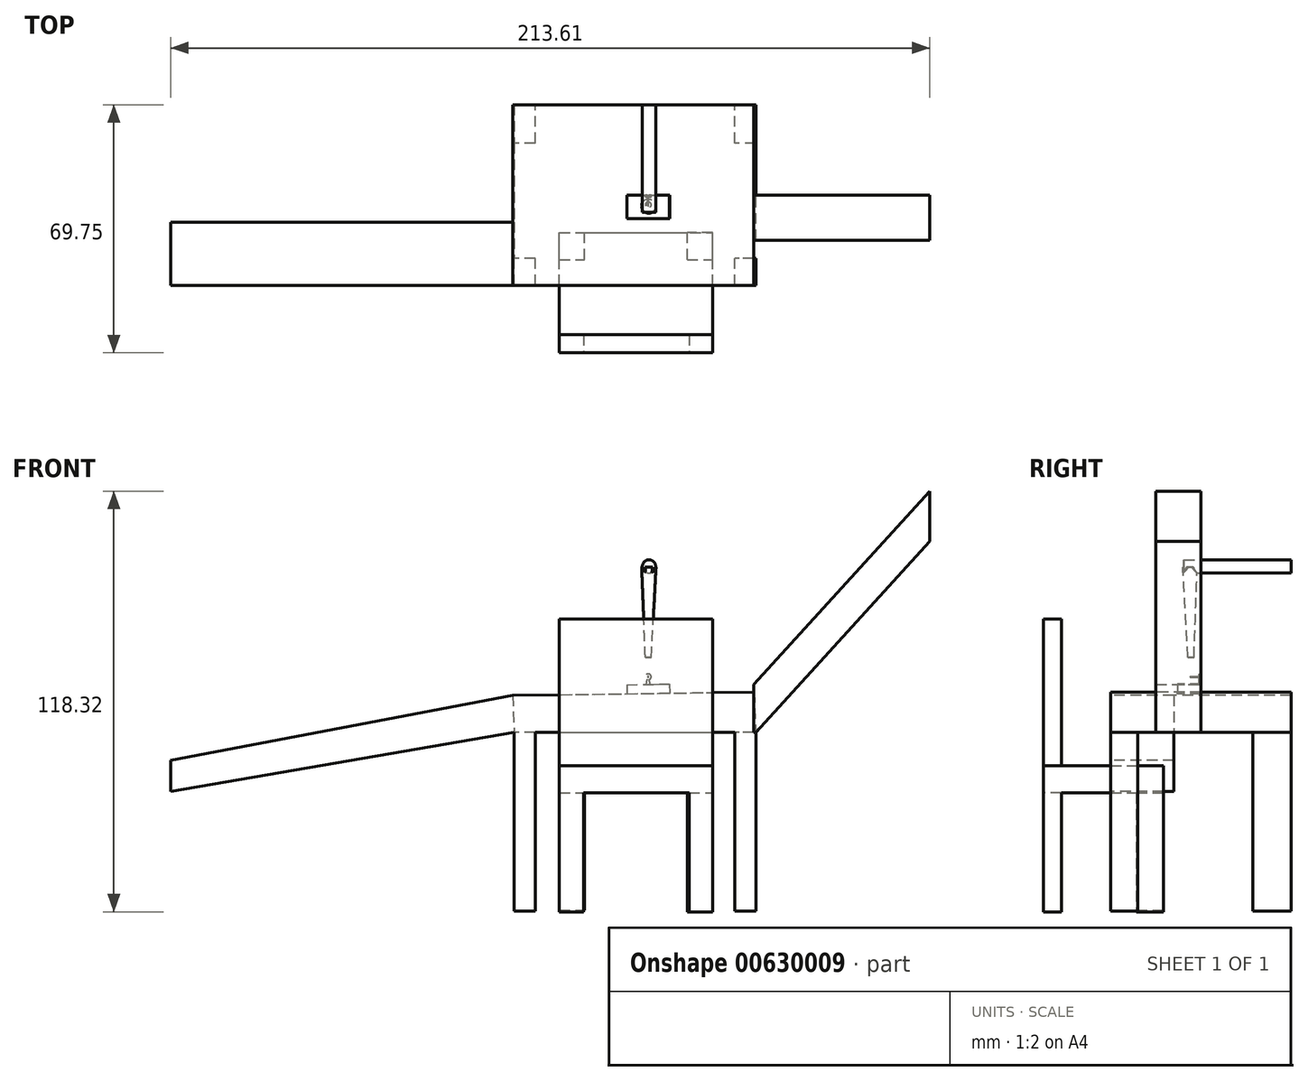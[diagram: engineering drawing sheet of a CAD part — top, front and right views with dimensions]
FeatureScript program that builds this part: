
annotation { "Feature Type Name" : "Feature", "Feature Type Description" : "" }
export const myFeature = defineFeature(function(context is Context, id is Id, definition is map)
    precondition{}
    {
        {
            var Q0;
            Q0=qCreatedBy(makeId("Front.planeOp"),FACE);
            var sketch = newSketch(context, id + "F0", { "sketchPlane" : qUnion([Q0])});
            skLineSegment(sketch, "E0", {"start": v(61.58, 0) * mm, "end": v(111.12, 54.36) * mm});
            skLineSegment(sketch, "E1", {"start": v(111.12, 54.36) * mm, "end": v(111.12, 40.27) * mm});
            skLineSegment(sketch, "E2", {"start": v(111.12, 40.27) * mm, "end": v(62.19, -13.43) * mm});
            skLineSegment(sketch, "E3", {"start": v(62.19, -13.43) * mm, "end": v(0, -13.43) * mm});
            skLineSegment(sketch, "E4", {"start": v(0, -13.43) * mm, "end": v(0, 0) * mm});
            skLineSegment(sketch, "E5", {"start": v(0, 0) * mm, "end": v(61.58, 0) * mm});
            skLineSegment(sketch, "E6", {"start": v(61.58, 0) * mm, "end": v(62.19, -13.43) * mm});
            skSolve(sketch);
        }
        {
            var Q0;
            Q0=makeQuery(id+"F0.imprint","IMPRINT",FACE,{"disambiguationData":[TD([[makeQuery(id+"F0.imprint","IMPRINT",EDGE,{"derivedFrom":sQuery(id+"F0.wireOp",EDGE,"E0")}),-1.0]])]});
            extrude(context, id + "F1", {"entities" : qUnion([Q0]), "depth" : 12.7 * mm, "offsetDistance" : 25.4 * mm});
        }
        {
            var Q0;
            Q0=makeQuery(id+"F1.opExtrude","CAP_FACE",FACE,{"disambiguationData":[OSD([sQuery(id+"F0.wireOp",EDGE,"E0"),sQuery(id+"F0.wireOp",EDGE,"E1"),sQuery(id+"F0.wireOp",EDGE,"E2"),sQuery(id+"F0.wireOp",EDGE,"E6")])],"isStart":false});
            var sketch = newSketch(context, id + "F2", { "sketchPlane" : qUnion([Q0])});
            skLineSegment(sketch, "E7", {"start": v(61.58, 0) * mm, "end": v(-6.26, -3.07) * mm});
            skLineSegment(sketch, "E8", {"start": v(-6.26, -3.07) * mm, "end": v(-5.79, -13.43) * mm});
            skLineSegment(sketch, "E9", {"start": v(-5.79, -13.43) * mm, "end": v(62.19, -13.43) * mm});
            skLineSegment(sketch, "E10", {"start": v(62.19, -13.43) * mm, "end": v(61.58, 0) * mm});
            skSolve(sketch);
        }
        {
            var Q0;
            Q0=makeQuery(id+"F2.imprint","IMPRINT",FACE,{"disambiguationData":[TD([[makeQuery(id+"F2.imprint","IMPRINT",EDGE,{"derivedFrom":sQuery(id+"F2.wireOp",EDGE,"E7")}),1.0]])]});
            extrude(context, id + "F3", {"entities" : qUnion([Q0]), "operationType" : NewBodyOperationType.ADD, "oppositeDirection" : true, "depth" : 38.1 * mm, "offsetDistance" : 25.4 * mm});
        }
        {
            var Q0;
            Q0=makeQuery(id+"F3.boolean.opBoolean","MERGE",FACE,{"derivedFrom":[makeQuery(id+"F1.opExtrude","CAP_FACE",FACE,{"disambiguationData":[OSD([sQuery(id+"F0.wireOp",EDGE,"E0"),sQuery(id+"F0.wireOp",EDGE,"E1"),sQuery(id+"F0.wireOp",EDGE,"E2"),sQuery(id+"F0.wireOp",EDGE,"E6")])],"isStart":false}),makeQuery(id+"F3.opExtrude","CAP_FACE",FACE,{"disambiguationData":[OSD([sQuery(id+"F2.wireOp",EDGE,"E7"),sQuery(id+"F2.wireOp",EDGE,"E8"),sQuery(id+"F2.wireOp",EDGE,"E9"),sQuery(id+"F2.wireOp",EDGE,"E10")])],"isStart":true})]});
            var sketch = newSketch(context, id + "F4", { "sketchPlane" : qUnion([Q0])});
            skLineSegment(sketch, "E11", {"start": v(61.58, 0) * mm, "end": v(61.58, -13.43) * mm});
            skLineSegment(sketch, "E12", {"start": v(61.58, -13.43) * mm, "end": v(-5.79, -13.43) * mm});
            skLineSegment(sketch, "E13", {"start": v(-5.79, -13.43) * mm, "end": v(-6.26, -3.07) * mm});
            skLineSegment(sketch, "E14", {"start": v(-6.26, -3.07) * mm, "end": v(61.58, 0) * mm});
            skSolve(sketch);
        }
        {
            var Q0;
            Q0=makeQuery(id+"F4.imprint","IMPRINT",FACE,{"disambiguationData":[TD([[makeQuery(id+"F4.imprint","IMPRINT",EDGE,{"derivedFrom":sQuery(id+"F4.wireOp",EDGE,"E11")}),-1.0]])]});
            extrude(context, id + "F5", {"entities" : qUnion([Q0]), "operationType" : NewBodyOperationType.ADD, "depth" : 12.7 * mm, "offsetDistance" : 25.4 * mm});
        }
        {
            var Q0;
            Q0=makeQuery(id+"F5.opExtrude","CAP_FACE",FACE,{"disambiguationData":[OSD([sQuery(id+"F4.wireOp",EDGE,"E11"),sQuery(id+"F4.wireOp",EDGE,"E12"),sQuery(id+"F4.wireOp",EDGE,"E13"),sQuery(id+"F4.wireOp",EDGE,"E14")])],"isStart":false});
            var sketch = newSketch(context, id + "F6", { "sketchPlane" : qUnion([Q0])});
            skLineSegment(sketch, "E15", {"start": v(-6.26, -3.07) * mm, "end": v(61.58, -2.1) * mm});
            skLineSegment(sketch, "E16", {"start": v(61.58, -2.1) * mm, "end": v(61.58, 0) * mm});
            skLineSegment(sketch, "E17", {"start": v(61.58, 0) * mm, "end": v(-6.26, -3.07) * mm});
            skSolve(sketch);
        }
        {
            var Q0;
            Q0=makeQuery(id+"F6.imprint","IMPRINT",FACE,{"disambiguationData":[TD([[makeQuery(id+"F6.imprint","IMPRINT",EDGE,{"derivedFrom":sQuery(id+"F6.wireOp",EDGE,"E15")}),1.0]])]});
            extrude(context, id + "F7", {"entities" : qUnion([Q0]), "operationType" : NewBodyOperationType.REMOVE, "oppositeDirection" : true, "depth" : 127 * mm, "offsetDistance" : 25.4 * mm});
        }
        {
            var Q0;
            Q0=makeQuery(id+"F7.boolean.opBoolean","COPY",FACE,{"derivedFrom":makeQuery(id+"F7.opExtrude","SWEPT_FACE",FACE,{"disambiguationData":[OSD([sQuery(id+"F6.wireOp",EDGE,"E16")])]})});
            var sketch = newSketch(context, id + "F8", { "sketchPlane" : qUnion([Q0])});
            skLineSegment(sketch, "E18", {"start": v(12.7, 0) * mm, "end": v(-25.4, 0) * mm});
            skLineSegment(sketch, "E19", {"start": v(-25.4, 0) * mm, "end": v(-25.4, -2.1) * mm});
            skLineSegment(sketch, "E20", {"start": v(-25.4, -2.1) * mm, "end": v(12.7, -2.1) * mm});
            skLineSegment(sketch, "E21", {"start": v(12.7, -2.1) * mm, "end": v(12.7, 0) * mm});
            skLineSegment(sketch, "E22", {"start": v(0, 0) * mm, "end": v(0, -2.1) * mm});
            skSolve(sketch);
        }
        {
            var Q0;
            {var subQ0=sQuery(id+"F8.wireOp",EDGE,"E19");Q0=makeQuery(id+"F8.imprint","IMPRINT",FACE,{"disambiguationData":[TD([[makeQuery(id+"F8.imprint","IMPRINT",EDGE,{"derivedFrom":subQ0}),1.0]])]});}
            extrude(context, id + "F9", {"entities" : qUnion([Q0]), "operationType" : NewBodyOperationType.REMOVE, "oppositeDirection" : true, "depth" : 25.4 * mm, "offsetDistance" : 25.4 * mm});
        }
        {
            var Q0;
            Q0=makeQuery(id+"F7.boolean.opBoolean","COPY",FACE,{"derivedFrom":makeQuery(id+"F7.opExtrude","SWEPT_FACE",FACE,{"disambiguationData":[OSD([sQuery(id+"F6.wireOp",EDGE,"E15")])]})});
            var sketch = newSketch(context, id + "F10", { "sketchPlane" : qUnion([Q0])});
            skLineSegment(sketch, "E23.bottom", {"start": v(25.86, 0) * mm, "end": v(37.88, 0) * mm});
            skLineSegment(sketch, "E23.top", {"start": v(25.86, -9.18) * mm, "end": v(37.88, -9.18) * mm});
            skLineSegment(sketch, "E23.left", {"start": v(25.86, 0) * mm, "end": v(25.86, -9.18) * mm});
            skLineSegment(sketch, "E23.right", {"start": v(37.88, 0) * mm, "end": v(37.88, -9.18) * mm});
            skSolve(sketch);
        }
        {
            var Q0;
            Q0=makeQuery(id+"F10.imprint","IMPRINT",FACE,{"disambiguationData":[TD([[makeQuery(id+"F10.imprint","IMPRINT",EDGE,{"derivedFrom":sQuery(id+"F10.wireOp",EDGE,"E23.bottom")}),-1.0]])]});
            extrude(context, id + "F11", {"entities" : qUnion([Q0]), "operationType" : NewBodyOperationType.ADD, "depth" : 2.54 * mm, "offsetDistance" : 25.4 * mm});
        }
        {
            var Q0;
            Q0=makeQuery(id+"F11.opExtrude","SWEPT_FACE",FACE,{"disambiguationData":[OSD([sQuery(id+"F10.wireOp",EDGE,"E23.bottom")])]});
            var sketch = newSketch(context, id + "F12", { "sketchPlane" : qUnion([Q0])});
            skLineSegment(sketch, "E24", {"start": v(-31.91, -2.53) * mm, "end": v(-31.91, 2.15) * mm});
            skCircle(sketch, "E25", {"center": v(-31.91, 2.15) * mm, "radius": 0.83 * mm});
            skLineSegment(sketch, "E26", {"start": v(-31.91, -2.53) * mm, "end": v(-33.19, -2.5) * mm});
            skLineSegment(sketch, "E27", {"start": v(-33.19, -2.5) * mm, "end": v(-31.91, 2.15) * mm});
            skLineSegment(sketch, "E28.MirrorCS", {"start": v(-30.64, -2.5) * mm, "end": v(-31.91, 2.15) * mm});
            skLineSegment(sketch, "E29.MirrorCS", {"start": v(-31.91, -2.53) * mm, "end": v(-30.64, -2.5) * mm});
            skSolve(sketch);
        }
        {
            var Q0;
            {var subQ0=sQuery(id+"F12.wireOp",EDGE,"E25");var subQ1=sQuery(id+"F12.wireOp",EDGE,"E24");var subQ2=makeQuery(id+"F12.imprint","INTERSECT",VERTEX,{"derivedFrom":[subQ1,subQ0]});Q0=makeQuery(id+"F12.imprint","IMPRINT",FACE,{"disambiguationData":[TD([[makeQuery(id+"F12.imprint","IMPRINT",EDGE,{"disambiguationData":[TD([[subQ2,1.0]])],"derivedFrom":subQ1}),-1.0]])]});}
            var Q1;
            {var subQ0=sQuery(id+"F12.wireOp",EDGE,"E25");var subQ1=sQuery(id+"F12.wireOp",EDGE,"E24");var subQ2=makeQuery(id+"F12.imprint","INTERSECT",VERTEX,{"derivedFrom":[subQ1,subQ0]});Q1=makeQuery(id+"F12.imprint","IMPRINT",FACE,{"disambiguationData":[TD([[makeQuery(id+"F12.imprint","IMPRINT",EDGE,{"disambiguationData":[TD([[subQ2,1.0]])],"derivedFrom":subQ1}),1.0]])]});}
            var Q2;
            {var subQ0=sQuery(id+"F12.wireOp",EDGE,"E27");var subQ3=sQuery(id+"F12.wireOp",EDGE,"E25");var subQ5=makeQuery(id+"F12.imprint","INTERSECT",VERTEX,{"derivedFrom":[subQ3,subQ0]});Q2=makeQuery(id+"F12.imprint","IMPRINT",FACE,{"disambiguationData":[TD([[makeQuery(id+"F12.imprint","IMPRINT",EDGE,{"disambiguationData":[TD([[subQ5,-1.0]])],"derivedFrom":subQ3}),1.0]])]});}
            var Q3;
            {var subQ0=sQuery(id+"F12.wireOp",EDGE,"E28.MirrorCS");var subQ3=sQuery(id+"F12.wireOp",EDGE,"E25");var subQ5=makeQuery(id+"F12.imprint","INTERSECT",VERTEX,{"derivedFrom":[subQ3,subQ0]});Q3=makeQuery(id+"F12.imprint","IMPRINT",FACE,{"disambiguationData":[TD([[makeQuery(id+"F12.imprint","IMPRINT",EDGE,{"disambiguationData":[TD([[subQ5,1.0]])],"derivedFrom":subQ3}),1.0]])]});}
            var Q4;
            {var subQ0=sQuery(id+"F12.wireOp",EDGE,"E27");var subQ1=sQuery(id+"F12.wireOp",EDGE,"E25");var subQ2=makeQuery(id+"F12.imprint","INTERSECT",VERTEX,{"derivedFrom":[subQ1,subQ0]});Q4=makeQuery(id+"F12.imprint","IMPRINT",FACE,{"disambiguationData":[TD([[makeQuery(id+"F12.imprint","IMPRINT",EDGE,{"disambiguationData":[TD([[subQ2,1.0]])],"derivedFrom":subQ1}),1.0]])]});}
            extrude(context, id + "F13", {"entities" : qUnion([Q0, Q1, Q2, Q3, Q4]), "operationType" : NewBodyOperationType.ADD, "oppositeDirection" : true, "depth" : 0.5 * mm, "offsetDistance" : 25.4 * mm});
        }
        {
            var Q0;
            Q0=makeQuery(id+"F13.opExtrude","CAP_FACE",FACE,{"disambiguationData":[OSD([sQuery(id+"F10.wireOp",EDGE,"E23.bottom"),sQuery(id+"F12.wireOp",EDGE,"E25"),sQuery(id+"F12.wireOp",EDGE,"E27"),sQuery(id+"F12.wireOp",EDGE,"E28.MirrorCS")])],"isStart":false});
            var sketch = newSketch(context, id + "F14", { "sketchPlane" : qUnion([Q0])});
            skCircle(sketch, "E30", {"center": v(31.91, 2.15) * mm, "radius": 0.16 * mm});
            skSolve(sketch);
        }
        {
            var Q0;
            Q0=makeQuery(id+"F14.imprint","IMPRINT",FACE,{"disambiguationData":[TD([[makeQuery(id+"F14.imprint","IMPRINT",EDGE,{"derivedFrom":sQuery(id+"F14.wireOp",EDGE,"E30")}),1.0]])]});
            extrude(context, id + "F15", {"entities" : qUnion([Q0]), "operationType" : NewBodyOperationType.ADD, "depth" : 2.54 * mm, "offsetDistance" : 25.4 * mm});
        }
        {
            var Q0;
            Q0=makeQuery(id+"F11.opExtrude","SWEPT_FACE",FACE,{"disambiguationData":[OSD([sQuery(id+"F10.wireOp",EDGE,"E23.top")])]});
            extrude(context, id + "F16", {"entities" : qUnion([Q0]), "operationType" : NewBodyOperationType.REMOVE, "oppositeDirection" : true, "depth" : 2.54 * mm, "offsetDistance" : 25.4 * mm});
        }
        {
            var Q0;
            Q0=makeQuery(id+"F3.opExtrude","CAP_FACE",FACE,{"disambiguationData":[OSD([sQuery(id+"F2.wireOp",EDGE,"E7"),sQuery(id+"F2.wireOp",EDGE,"E8"),sQuery(id+"F2.wireOp",EDGE,"E9"),sQuery(id+"F2.wireOp",EDGE,"E10")])],"isStart":false});
            var sketch = newSketch(context, id + "F17", { "sketchPlane" : qUnion([Q0])});
            skLineSegment(sketch, "E31", {"start": v(-62.19, -13.43) * mm, "end": v(-62.19, -63.77) * mm});
            skLineSegment(sketch, "E32", {"start": v(-62.19, -63.77) * mm, "end": v(-56.29, -63.77) * mm});
            skLineSegment(sketch, "E33", {"start": v(-56.29, -63.77) * mm, "end": v(-56.29, -13.43) * mm});
            skLineSegment(sketch, "E34", {"start": v(-56.29, -13.43) * mm, "end": v(-62.19, -13.43) * mm});
            skLineSegment(sketch, "E35", {"start": v(-28.2, -13.43) * mm, "end": v(-28.2, -2.58) * mm});
            skLineSegment(sketch, "E36.MirrorCS", {"start": v(-0.11, -63.77) * mm, "end": v(-0.11, -13.43) * mm});
            skLineSegment(sketch, "E37.MirrorCS", {"start": v(5.79, -13.43) * mm, "end": v(5.79, -63.77) * mm});
            skLineSegment(sketch, "E38.MirrorCS", {"start": v(5.79, -63.77) * mm, "end": v(-0.11, -63.77) * mm});
            skSolve(sketch);
        }
        {
            var Q0;
            {var subQ0=sQuery(id+"F17.wireOp",EDGE,"E36.MirrorCS");Q0=makeQuery(id+"F17.imprint","IMPRINT",FACE,{"disambiguationData":[TD([[makeQuery(id+"F17.imprint","IMPRINT",EDGE,{"derivedFrom":subQ0}),-1.0]])]});}
            var Q1;
            Q1=makeQuery(id+"F17.imprint","IMPRINT",FACE,{"disambiguationData":[TD([[makeQuery(id+"F17.imprint","IMPRINT",EDGE,{"derivedFrom":sQuery(id+"F17.wireOp",EDGE,"E31")}),1.0]])]});
            extrude(context, id + "F18", {"entities" : qUnion([Q0, Q1]), "operationType" : NewBodyOperationType.ADD, "oppositeDirection" : true, "depth" : 50.8 * mm, "offsetDistance" : 25.4 * mm});
        }
        {
            var Q0;
            Q0=makeQuery(id+"F18.opExtrude","SWEPT_FACE",FACE,{"disambiguationData":[OSD([sQuery(id+"F17.wireOp",EDGE,"E37.MirrorCS")])]});
            var sketch = newSketch(context, id + "F19", { "sketchPlane" : qUnion([Q0])});
            skLineSegment(sketch, "E39", {"start": v(17.83, -63.77) * mm, "end": v(17.83, -13.43) * mm});
            skLineSegment(sketch, "E40", {"start": v(17.83, -13.43) * mm, "end": v(-14.62, -13.43) * mm});
            skLineSegment(sketch, "E41", {"start": v(-14.62, -13.43) * mm, "end": v(-14.62, -63.77) * mm});
            skLineSegment(sketch, "E42", {"start": v(-14.62, -63.77) * mm, "end": v(17.83, -63.77) * mm});
            skSolve(sketch);
        }
        {
            var Q0;
            Q0=makeQuery(id+"F19.imprint","IMPRINT",FACE,{"disambiguationData":[TD([[makeQuery(id+"F19.imprint","IMPRINT",EDGE,{"derivedFrom":sQuery(id+"F19.wireOp",EDGE,"E39")}),1.0]])]});
            extrude(context, id + "F20", {"entities" : qUnion([Q0]), "operationType" : NewBodyOperationType.REMOVE, "oppositeDirection" : true, "depth" : 304.8 * mm, "offsetDistance" : 25.4 * mm});
        }
        {
            var Q0;
            Q0=makeQuery(id+"F18.boolean.opBoolean","MERGE",FACE,{"derivedFrom":[makeQuery(id+"F5.opExtrude","CAP_FACE",FACE,{"disambiguationData":[OSD([sQuery(id+"F4.wireOp",EDGE,"E11"),sQuery(id+"F4.wireOp",EDGE,"E12"),sQuery(id+"F4.wireOp",EDGE,"E13"),sQuery(id+"F4.wireOp",EDGE,"E14")])],"isStart":false}),makeQuery(id+"F18.opExtrude","CAP_FACE",FACE,{"disambiguationData":[OSD([sQuery(id+"F17.wireOp",EDGE,"E31"),sQuery(id+"F17.wireOp",EDGE,"E32"),sQuery(id+"F17.wireOp",EDGE,"E33"),sQuery(id+"F17.wireOp",EDGE,"E34")])],"isStart":false}),makeQuery(id+"F18.opExtrude","CAP_FACE",FACE,{"disambiguationData":[OSD([sQuery(id+"F2.wireOp",EDGE,"E9"),sQuery(id+"F17.wireOp",EDGE,"E36.MirrorCS"),sQuery(id+"F17.wireOp",EDGE,"E37.MirrorCS"),sQuery(id+"F17.wireOp",EDGE,"E38.MirrorCS")])],"isStart":false})]});
            var sketch = newSketch(context, id + "F21", { "sketchPlane" : qUnion([Q0])});
            skLineSegment(sketch, "E43", {"start": v(-6.26, -3.07) * mm, "end": v(-102.5, -21.32) * mm});
            skLineSegment(sketch, "E44", {"start": v(-102.5, -21.32) * mm, "end": v(-102.5, -30.14) * mm});
            skLineSegment(sketch, "E45", {"start": v(-102.5, -30.14) * mm, "end": v(-5.79, -13.43) * mm});
            skLineSegment(sketch, "E46", {"start": v(-5.79, -13.43) * mm, "end": v(-6.26, -3.07) * mm});
            skSolve(sketch);
        }
        {
            var Q0;
            Q0 = qSketchRegion(id + "F21", true);
            extrude(context, id + "F22", {"entities" : qUnion([Q0]), "operationType" : NewBodyOperationType.ADD, "oppositeDirection" : true, "depth" : 17.78 * mm, "offsetDistance" : 25.4 * mm});
        }
        {
            var Q0;
            Q0=qCreatedBy(makeId("Top.planeOp"),FACE);
            cPlane(context, id + "F23", {"entities" : qUnion([Q0]), "cplaneType" : CPlaneType.OFFSET, "offset" : 22.86 * mm, "oppositeDirection" : true, "width" : 152.4 * mm, "height" : 152.4 * mm});
        }
        {
            var Q0;
            Q0=qCreatedBy(id+"F23.planeOp",FACE);
            var sketch = newSketch(context, id + "F24", { "sketchPlane" : qUnion([Q0])});
            skLineSegment(sketch, "E47.bottom", {"start": v(6.89, -44.35) * mm, "end": v(50.02, -44.35) * mm});
            skLineSegment(sketch, "E47.top", {"start": v(6.89, -10.54) * mm, "end": v(50.02, -10.54) * mm});
            skLineSegment(sketch, "E47.left", {"start": v(6.89, -44.35) * mm, "end": v(6.89, -10.54) * mm});
            skLineSegment(sketch, "E47.right", {"start": v(50.02, -44.35) * mm, "end": v(50.02, -10.54) * mm});
            skSolve(sketch);
        }
        {
            var Q0;
            Q0 = qSketchRegion(id + "F24", true);
            extrude(context, id + "F25", {"entities" : qUnion([Q0]), "oppositeDirection" : true, "depth" : 7.62 * mm, "offsetDistance" : 25.4 * mm});
        }
        {
            var Q0;
            Q0=makeQuery(id+"F25.opExtrude","SWEPT_FACE",FACE,{"disambiguationData":[OSD([sQuery(id+"F24.wireOp",EDGE,"E47.bottom")])]});
            var sketch = newSketch(context, id + "F26", { "sketchPlane" : qUnion([Q0])});
            skLineSegment(sketch, "E48", {"start": v(50.02, -30.48) * mm, "end": v(50.02, 18.38) * mm});
            skLineSegment(sketch, "E49", {"start": v(50.02, 18.38) * mm, "end": v(6.89, 18.38) * mm});
            skLineSegment(sketch, "E50", {"start": v(6.89, 18.38) * mm, "end": v(6.89, -30.48) * mm});
            skLineSegment(sketch, "E51", {"start": v(6.89, -30.48) * mm, "end": v(50.02, -30.48) * mm});
            skLineSegment(sketch, "E52", {"start": v(50.02, -30.48) * mm, "end": v(50.02, -63.47) * mm});
            skLineSegment(sketch, "E53", {"start": v(50.02, -63.47) * mm, "end": v(44.38, -63.47) * mm});
            skLineSegment(sketch, "E54", {"start": v(44.38, -63.47) * mm, "end": v(44.38, -30.48) * mm});
            skLineSegment(sketch, "E55", {"start": v(44.38, -30.48) * mm, "end": v(50.02, -30.48) * mm});
            skLineSegment(sketch, "E56", {"start": v(28.45, -30.48) * mm, "end": v(28.45, -22.86) * mm});
            skLineSegment(sketch, "E57.MirrorCS", {"start": v(6.89, -30.48) * mm, "end": v(6.89, -63.47) * mm});
            skLineSegment(sketch, "E58.MirrorCS", {"start": v(12.52, -63.47) * mm, "end": v(12.52, -30.48) * mm});
            skLineSegment(sketch, "E59.MirrorCS", {"start": v(12.52, -30.48) * mm, "end": v(6.89, -30.48) * mm});
            skLineSegment(sketch, "E60.MirrorCS", {"start": v(6.89, -63.47) * mm, "end": v(12.52, -63.47) * mm});
            skSolve(sketch);
        }
        {
            var Q0;
            {var subQ4=sQuery(id+"F26.wireOp",EDGE,"E49");Q0=makeQuery(id+"F26.imprint","IMPRINT",FACE,{"disambiguationData":[TD([[makeQuery(id+"F26.imprint","IMPRINT",EDGE,{"derivedFrom":subQ4}),1.0]])]});}
            extrude(context, id + "F27", {"entities" : qUnion([Q0]), "oppositeDirection" : true, "depth" : 5.08 * mm, "offsetDistance" : 25.4 * mm});
        }
        {
            var Q0;
            Q0=makeQuery(id+"F25.opExtrude","SWEPT_FACE",FACE,{"disambiguationData":[OSD([sQuery(id+"F24.wireOp",EDGE,"E47.bottom")])]});
            var sketch = newSketch(context, id + "F28", { "sketchPlane" : qUnion([Q0])});
            skLineSegment(sketch, "E61.bottom", {"start": v(50.02, -30.48) * mm, "end": v(43.4, -30.48) * mm});
            skLineSegment(sketch, "E61.top", {"start": v(50.02, -63.96) * mm, "end": v(43.4, -63.96) * mm});
            skLineSegment(sketch, "E61.left", {"start": v(50.02, -30.48) * mm, "end": v(50.02, -63.96) * mm});
            skLineSegment(sketch, "E61.right", {"start": v(43.4, -30.48) * mm, "end": v(43.4, -63.96) * mm});
            skLineSegment(sketch, "E62.bottom", {"start": v(6.89, -30.48) * mm, "end": v(13.75, -30.48) * mm});
            skLineSegment(sketch, "E62.top", {"start": v(6.89, -63.96) * mm, "end": v(13.75, -63.96) * mm});
            skLineSegment(sketch, "E62.left", {"start": v(6.89, -30.48) * mm, "end": v(6.89, -63.96) * mm});
            skLineSegment(sketch, "E62.right", {"start": v(13.75, -30.48) * mm, "end": v(13.75, -63.96) * mm});
            skSolve(sketch);
        }
        {
            var Q0;
            Q0 = qSketchRegion(id + "F28", true);
            extrude(context, id + "F29", {"entities" : qUnion([Q0]), "operationType" : NewBodyOperationType.ADD, "oppositeDirection" : true, "depth" : 5.08 * mm, "offsetDistance" : 25.4 * mm});
        }
        {
            var Q0;
            Q0=makeQuery(id+"F25.opExtrude","SWEPT_FACE",FACE,{"disambiguationData":[OSD([sQuery(id+"F24.wireOp",EDGE,"E47.top")])]});
            var sketch = newSketch(context, id + "F30", { "sketchPlane" : qUnion([Q0])});
            skLineSegment(sketch, "E63.bottom", {"start": v(-50.02, -30.48) * mm, "end": v(-42.9, -30.48) * mm});
            skLineSegment(sketch, "E63.top", {"start": v(-50.02, -63.96) * mm, "end": v(-42.9, -63.96) * mm});
            skLineSegment(sketch, "E63.left", {"start": v(-50.02, -30.48) * mm, "end": v(-50.02, -63.96) * mm});
            skLineSegment(sketch, "E63.right", {"start": v(-42.9, -30.48) * mm, "end": v(-42.9, -63.96) * mm});
            skLineSegment(sketch, "E64.bottom", {"start": v(-6.89, -30.48) * mm, "end": v(-14, -30.48) * mm});
            skLineSegment(sketch, "E64.top", {"start": v(-6.89, -63.47) * mm, "end": v(-14, -63.47) * mm});
            skLineSegment(sketch, "E64.left", {"start": v(-6.89, -30.48) * mm, "end": v(-6.89, -63.47) * mm});
            skLineSegment(sketch, "E64.right", {"start": v(-14, -30.48) * mm, "end": v(-14, -63.47) * mm});
            skSolve(sketch);
        }
        {
            var Q0;
            Q0 = qSketchRegion(id + "F30", true);
            extrude(context, id + "F31", {"entities" : qUnion([Q0]), "operationType" : NewBodyOperationType.ADD, "oppositeDirection" : true, "depth" : 7.62 * mm, "offsetDistance" : 25.4 * mm});
        }
        {
            var Q0;
            Q0=qCreatedBy(makeId("Top.planeOp"),FACE);
            cPlane(context, id + "F32", {"entities" : qUnion([Q0]), "cplaneType" : CPlaneType.OFFSET, "offset" : 7.62 * mm, "width" : 152.4 * mm, "height" : 152.4 * mm});
        }
        {
            var Q0;
            Q0=qCreatedBy(id+"F32.planeOp",FACE);
            var sketch = newSketch(context, id + "F33", { "sketchPlane" : qUnion([Q0])});
            skCircle(sketch, "E65", {"center": v(31.93, -2.8) * mm, "radius": 0.85 * mm});
            skSolve(sketch);
        }
        {
            var Q0;
            Q0=qCreatedBy(id+"F32.planeOp",FACE);
            cPlane(context, id + "F34", {"entities" : qUnion([Q0]), "cplaneType" : CPlaneType.OFFSET, "offset" : 25.4 * mm, "width" : 152.4 * mm, "height" : 152.4 * mm});
        }
        {
            var Q0;
            Q0=qCreatedBy(id+"F34.planeOp",FACE);
            var sketch = newSketch(context, id + "F35", { "sketchPlane" : qUnion([Q0])});
            skCircle(sketch, "E66", {"center": v(32.08, -3.08) * mm, "radius": 2.03 * mm});
            skSolve(sketch);
        }
        {
            var Q0;
            Q0=makeQuery(id+"F35.imprint","IMPRINT",FACE,{"disambiguationData":[TD([[makeQuery(id+"F35.imprint","IMPRINT",EDGE,{"derivedFrom":sQuery(id+"F35.wireOp",EDGE,"E66")}),1.0]])]});
            var Q1;
            Q1=makeQuery(id+"F33.imprint","IMPRINT",FACE,{"disambiguationData":[TD([[makeQuery(id+"F33.imprint","IMPRINT",EDGE,{"derivedFrom":sQuery(id+"F33.wireOp",EDGE,"E65")}),1.0]])]});
            loft(context, id + "F36", {"sheetProfilesArray" : [{ "sheetProfileEntities" : qUnion([Q0]) }, { "sheetProfileEntities" : qUnion([Q1]) }]});
        }
        {
            var Q0;
            Q0=qCreatedBy(makeId("Front.planeOp"),FACE);
            cPlane(context, id + "F37", {"entities" : qUnion([Q0]), "cplaneType" : CPlaneType.OFFSET, "offset" : 12.7 * mm, "oppositeDirection" : true, "width" : 152.4 * mm, "height" : 152.4 * mm});
        }
        {
            var Q0;
            Q0=qCreatedBy(id+"F37.planeOp",FACE);
            cPlane(context, id + "F38", {"entities" : qUnion([Q0]), "cplaneType" : CPlaneType.OFFSET, "offset" : 12.7 * mm, "oppositeDirection" : true, "width" : 152.4 * mm, "height" : 152.4 * mm});
        }
        {
            var Q0;
            Q0=qCreatedBy(id+"F38.planeOp",FACE);
            var sketch = newSketch(context, id + "F39", { "sketchPlane" : qUnion([Q0])});
            skCircle(sketch, "E67", {"center": v(32.14, 33.22) * mm, "radius": 1.87 * mm});
            skSolve(sketch);
        }
        {
            var Q0;
            Q0=makeQuery(id+"F39.imprint","IMPRINT",FACE,{"disambiguationData":[TD([[makeQuery(id+"F39.imprint","IMPRINT",EDGE,{"derivedFrom":sQuery(id+"F39.wireOp",EDGE,"E67")}),1.0]])]});
            extrude(context, id + "F40", {"entities" : qUnion([Q0]), "operationType" : NewBodyOperationType.ADD, "depth" : 30.23 * mm, "offsetDistance" : 25.4 * mm});
        }
    });
